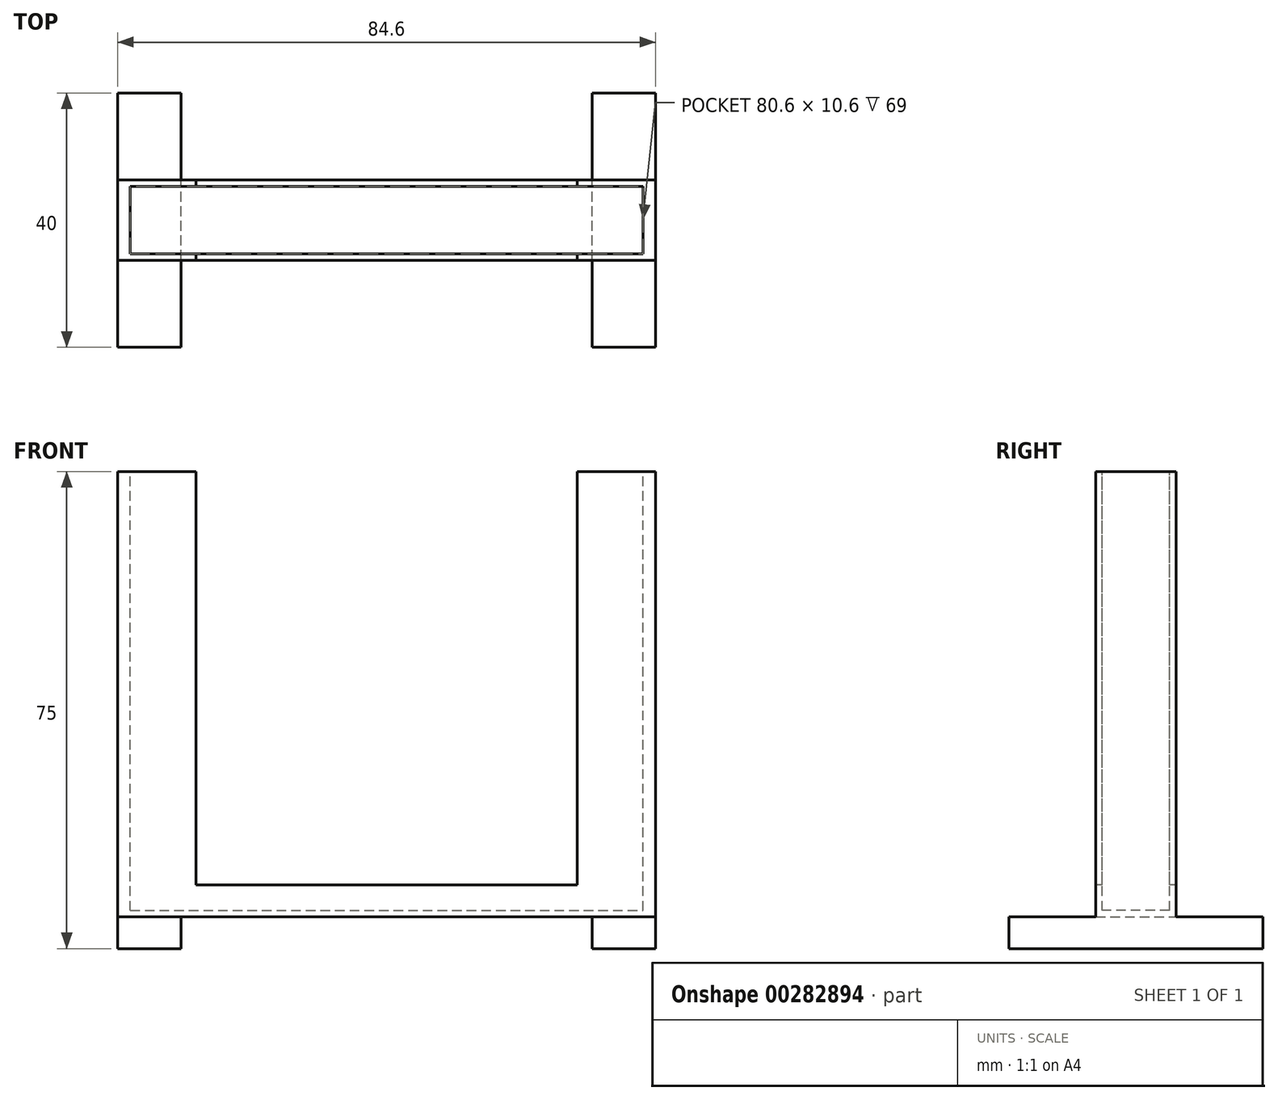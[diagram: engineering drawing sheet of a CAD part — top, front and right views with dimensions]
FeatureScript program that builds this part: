
annotation { "Feature Type Name" : "Feature", "Feature Type Description" : "" }
export const myFeature = defineFeature(function(context is Context, id is Id, definition is map)
    precondition{}
    {
        {
            var Q0;
            Q0=qCreatedBy(makeId("Front.planeOp"),FACE);
            var sketch = newSketch(context, id + "F0", { "sketchPlane" : qUnion([Q0])});
            skLineSegment(sketch, "E0.bottom", {"start": v(-42.3, 35) * mm, "end": v(42.3, 35) * mm});
            skLineSegment(sketch, "E0.top", {"start": v(-42.3, -35) * mm, "end": v(42.3, -35) * mm});
            skLineSegment(sketch, "E0.left", {"start": v(-42.3, 35) * mm, "end": v(-42.3, -35) * mm});
            skLineSegment(sketch, "E0.right", {"start": v(42.3, 35) * mm, "end": v(42.3, -35) * mm});
            skPoint(sketch, "E0.middle", {"position": v(0, 0) * mm});
            skSolve(sketch);
        }
        {
            var Q0;
            Q0 = qSketchRegion(id + "F0", true);
            extrude(context, id + "F1", {"entities" : qUnion([Q0]), "depth" : 6.3 * mm});
        }
        {
            var Q0;
            Q0 = qSketchRegion(id + "F0", true);
            extrude(context, id + "F2", {"entities" : qUnion([Q0]), "operationType" : NewBodyOperationType.ADD, "oppositeDirection" : true, "depth" : 6.3 * mm});
        }
        {
            var Q0;
            {var subQ0=sQuery(id+"F0.wireOp",EDGE,"E0.bottom");Q0=makeQuery(id+"F2.boolean.opBoolean","MERGE",FACE,{"derivedFrom":[makeQuery(id+"F1.opExtrude","SWEPT_FACE",FACE,{"disambiguationData":[OSD([subQ0])]}),makeQuery(id+"F2.opExtrude","SWEPT_FACE",FACE,{"disambiguationData":[OSD([subQ0])]})]});}
            var sketch = newSketch(context, id + "F3", { "sketchPlane" : qUnion([Q0])});
            skLineSegment(sketch, "E1.bottom", {"start": v(-40.3, 5.3) * mm, "end": v(40.3, 5.3) * mm});
            skLineSegment(sketch, "E1.top", {"start": v(-40.3, -5.3) * mm, "end": v(40.3, -5.3) * mm});
            skLineSegment(sketch, "E1.left", {"start": v(-40.3, 5.3) * mm, "end": v(-40.3, -5.3) * mm});
            skLineSegment(sketch, "E1.right", {"start": v(40.3, 5.3) * mm, "end": v(40.3, -5.3) * mm});
            skPoint(sketch, "E1.middle", {"position": v(0, 0) * mm});
            skSolve(sketch);
        }
        {
            var Q0;
            Q0 = qSketchRegion(id + "F3", true);
            extrude(context, id + "F4", {"entities" : qUnion([Q0]), "operationType" : NewBodyOperationType.REMOVE, "oppositeDirection" : true, "depth" : 69 * mm});
        }
        {
            var Q0;
            Q0=makeQuery(id+"F1.opExtrude","CAP_FACE",FACE,{"disambiguationData":[OSD([sQuery(id+"F0.wireOp",EDGE,"E0.bottom"),sQuery(id+"F0.wireOp",EDGE,"E0.top"),sQuery(id+"F0.wireOp",EDGE,"E0.left"),sQuery(id+"F0.wireOp",EDGE,"E0.right")])],"isStart":false});
            var sketch = newSketch(context, id + "F5", { "sketchPlane" : qUnion([Q0])});
            skLineSegment(sketch, "E2.top", {"start": v(-30, -30) * mm, "end": v(30, -30) * mm});
            skLineSegment(sketch, "E2.left", {"start": v(-30, 30) * mm, "end": v(-30, -30) * mm});
            skLineSegment(sketch, "E2.right", {"start": v(30, 30) * mm, "end": v(30, -30) * mm});
            skPoint(sketch, "E2.middle", {"position": v(0, 0) * mm});
            skLineSegment(sketch, "E3.top", {"start": v(-30, 35) * mm, "end": v(30, 35) * mm});
            skLineSegment(sketch, "E3.left", {"start": v(-30, -30) * mm, "end": v(-30, 35) * mm});
            skLineSegment(sketch, "E3.right", {"start": v(30, -30) * mm, "end": v(30, 35) * mm});
            skSolve(sketch);
        }
        {
            var Q0;
            Q0 = qSketchRegion(id + "F5", true);
            extrude(context, id + "F6", {"entities" : qUnion([Q0]), "operationType" : NewBodyOperationType.REMOVE, "oppositeDirection" : true, "depth" : 25 * mm});
        }
        {
            var Q0;
            {var subQ0=sQuery(id+"F0.wireOp",EDGE,"E0.top");Q0=makeQuery(id+"F2.boolean.opBoolean","MERGE",FACE,{"derivedFrom":[makeQuery(id+"F1.opExtrude","SWEPT_FACE",FACE,{"disambiguationData":[OSD([subQ0])]}),makeQuery(id+"F2.opExtrude","SWEPT_FACE",FACE,{"disambiguationData":[OSD([subQ0])]})]});}
            var sketch = newSketch(context, id + "F7", { "sketchPlane" : qUnion([Q0])});
            skLineSegment(sketch, "E4", {"start": v(-42.3, 0) * mm, "end": v(-37.3, 0) * mm, "construction": true});
            skLineSegment(sketch, "E5", {"start": v(42.3, 0) * mm, "end": v(37.3, 0) * mm, "construction": true});
            skLineSegment(sketch, "E6.bottom", {"start": v(-42.3, 20) * mm, "end": v(-32.3, 20) * mm});
            skLineSegment(sketch, "E6.top", {"start": v(-42.3, -20) * mm, "end": v(-32.3, -20) * mm});
            skLineSegment(sketch, "E6.left", {"start": v(-42.3, 20) * mm, "end": v(-42.3, -20) * mm});
            skLineSegment(sketch, "E6.right", {"start": v(-32.3, 20) * mm, "end": v(-32.3, -20) * mm});
            skPoint(sketch, "E6.middle", {"position": v(-37.3, 0) * mm});
            skLineSegment(sketch, "E7.bottom", {"start": v(32.3, 20) * mm, "end": v(42.3, 20) * mm});
            skLineSegment(sketch, "E7.top", {"start": v(32.3, -20) * mm, "end": v(42.3, -20) * mm});
            skLineSegment(sketch, "E7.left", {"start": v(32.3, 20) * mm, "end": v(32.3, -20) * mm});
            skLineSegment(sketch, "E7.right", {"start": v(42.3, 20) * mm, "end": v(42.3, -20) * mm});
            skPoint(sketch, "E7.middle", {"position": v(37.3, 0) * mm});
            skSolve(sketch);
        }
        {
            var Q0;
            Q0 = qSketchRegion(id + "F7", true);
            extrude(context, id + "F8", {"entities" : qUnion([Q0]), "operationType" : NewBodyOperationType.ADD, "depth" : 5 * mm});
        }
    });
